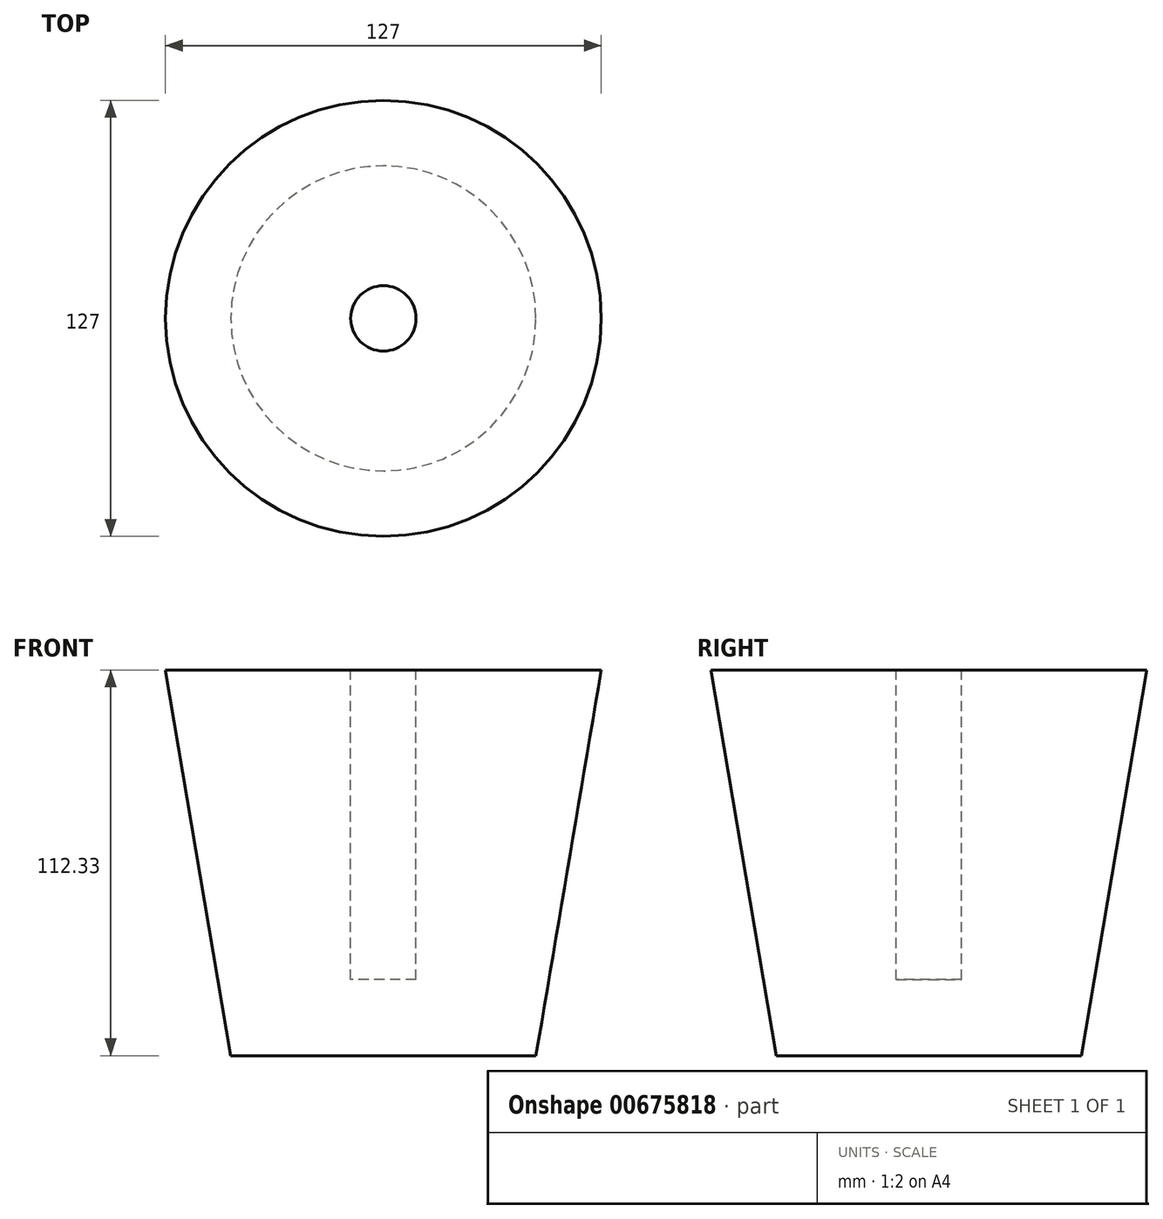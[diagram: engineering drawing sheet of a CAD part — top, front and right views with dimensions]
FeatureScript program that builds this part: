
annotation { "Feature Type Name" : "Feature", "Feature Type Description" : "" }
export const myFeature = defineFeature(function(context is Context, id is Id, definition is map)
    precondition{}
    {
        {
            var Q0;
            Q0=qCreatedBy(makeId("Front.planeOp"),FACE);
            var sketch = newSketch(context, id + "F0", { "sketchPlane" : qUnion([Q0])});
            skLineSegment(sketch, "E0", {"start": v(0, 61.75) * mm, "end": v(0, -50.58) * mm});
            skLineSegment(sketch, "E1", {"start": v(0, -50.58) * mm, "end": v(-44.45, -50.58) * mm});
            skLineSegment(sketch, "E2", {"start": v(-44.45, -50.58) * mm, "end": v(-63.5, 61.75) * mm});
            skLineSegment(sketch, "E3", {"start": v(-63.5, 61.75) * mm, "end": v(0, 61.75) * mm});
            skSolve(sketch);
        }
        {
            var Q0;
            Q0=makeQuery(id+"F0.imprint","IMPRINT",FACE,{"disambiguationData":[TD([[makeQuery(id+"F0.imprint","IMPRINT",EDGE,{"derivedFrom":sQuery(id+"F0.wireOp",EDGE,"E0")}),-1.0]])]});
            var Q1;
            Q1=sQuery(id+"F0.wireOp",EDGE,"E0");
            revolve(context, id + "F1", {"entities" : qUnion([Q0]), "axis" : qUnion([Q1]), "revolveType" : RevolveType.FULL});
        }
        {
            var Q0;
            Q0=makeQuery(id+"F1.opRevolve","SWEPT_FACE",FACE,{"disambiguationData":[OSD([sQuery(id+"F0.wireOp",EDGE,"E3")])]});
            var sketch = newSketch(context, id + "F2", { "sketchPlane" : qUnion([Q0])});
            skCircle(sketch, "E4", {"center": v(0, 0) * mm, "radius": 9.53 * mm});
            skSolve(sketch);
        }
        {
            var Q0;
            Q0=makeQuery(id+"F2.imprint","IMPRINT",FACE,{"disambiguationData":[TD([[makeQuery(id+"F2.imprint","IMPRINT",EDGE,{"derivedFrom":sQuery(id+"F2.wireOp",EDGE,"E4")}),1.0]])]});
            extrude(context, id + "F3", {"entities" : qUnion([Q0]), "operationType" : NewBodyOperationType.REMOVE, "oppositeDirection" : true, "depth" : 90.17 * mm, "offsetDistance" : 25.4 * mm});
        }
    });
